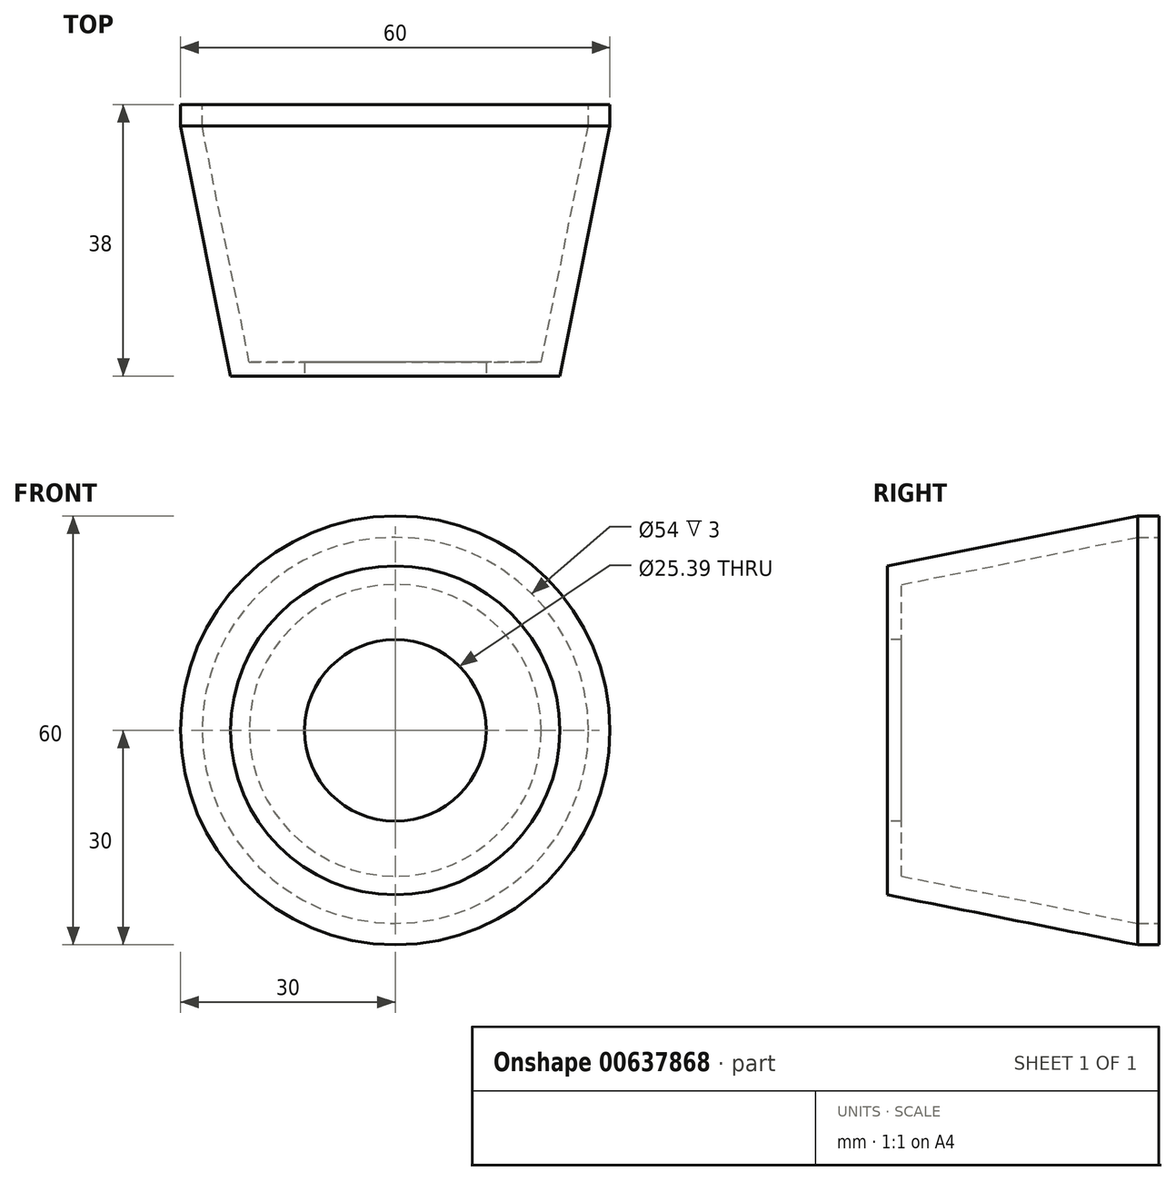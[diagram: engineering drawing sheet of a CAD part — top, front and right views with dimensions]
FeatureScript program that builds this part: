
annotation { "Feature Type Name" : "Feature", "Feature Type Description" : "" }
export const myFeature = defineFeature(function(context is Context, id is Id, definition is map)
    precondition{}
    {
        {
            var Q0;
            Q0=qCreatedBy(makeId("Front.planeOp"),FACE);
            var sketch = newSketch(context, id + "F0", { "sketchPlane" : qUnion([Q0])});
            skCircle(sketch, "E0", {"center": v(0, 0) * mm, "radius": 30 * mm});
            skCircle(sketch, "E1", {"center": v(0, 0) * mm, "radius": 27 * mm});
            skSolve(sketch);
        }
        {
            var Q0;
            Q0 = qSketchRegion(id + "F0", true);
            extrude(context, id + "F1", {"entities" : qUnion([Q0]), "depth" : 3 * mm, "offsetDistance" : 25 * mm});
        }
        {
            var Q0;
            Q0=qCreatedBy(makeId("Front.planeOp"),FACE);
            cPlane(context, id + "F2", {"entities" : qUnion([Q0]), "cplaneType" : CPlaneType.OFFSET, "offset" : 38 * mm, "width" : 150 * mm, "height" : 150 * mm});
        }
        {
            var Q0;
            Q0=qCreatedBy(id+"F2.planeOp",FACE);
            var sketch = newSketch(context, id + "F3", { "sketchPlane" : qUnion([Q0])});
            skCircle(sketch, "E2", {"center": v(0, 0) * mm, "radius": 23 * mm});
            skCircle(sketch, "E3", {"center": v(0, 0) * mm, "radius": 20 * mm, "construction": true});
            skSolve(sketch);
        }
        {
            var Q0;
            Q0=makeQuery(id+"F1.opExtrude","CAP_FACE",FACE,{"disambiguationData":[OSD([sQuery(id+"F0.wireOp",EDGE,"E0"),sQuery(id+"F0.wireOp",EDGE,"E1")])],"isStart":false});
            var sketch = newSketch(context, id + "F4", { "sketchPlane" : qUnion([Q0])});
            skCircle(sketch, "E4", {"center": v(0, 0) * mm, "radius": 30 * mm});
            skCircle(sketch, "E5", {"center": v(0, 0) * mm, "radius": 27 * mm, "construction": true});
            skSolve(sketch);
        }
        {
            var Q1;
            Q1 = qSketchRegion(id + "F4", true);
            var Q2;
            Q2 = qSketchRegion(id + "F3", true);
            loft(context, id + "F5", {"operationType" : NewBodyOperationType.ADD, "sheetProfilesArray" : [{ "sheetProfileEntities" : qUnion([Q1]) }, { "sheetProfileEntities" : qUnion([Q2]) }]});
        }
        {
            var Q0;
            Q0=makeQuery(id+"F5.opLoft","CAP_FACE",FACE,{"disambiguationData":[OSD([makeQuery(id+"F4.imprint","IMPRINT",FACE,{"disambiguationData":[TD([[makeQuery(id+"F4.imprint","IMPRINT",EDGE,{"derivedFrom":makeQuery(id+"F1.opExtrude","CAP_EDGE",EDGE,{"disambiguationData":[OSD([sQuery(id+"F0.wireOp",EDGE,"E1")])],"isStart":false})}),1.0]])]})])],"isStart":true});
            var sketch = newSketch(context, id + "F6", { "sketchPlane" : qUnion([Q0])});
            skCircle(sketch, "E6", {"center": v(0, 0) * mm, "radius": 27 * mm});
            skSolve(sketch);
        }
        {
            var Q0;
            Q0=makeQuery(id+"F5.opLoft","CAP_FACE",FACE,{"disambiguationData":[OSD([makeQuery(id+"F3.imprint","IMPRINT",FACE,{"disambiguationData":[TD([[makeQuery(id+"F3.imprint","IMPRINT",EDGE,{"derivedFrom":sQuery(id+"F3.wireOp",EDGE,"E2")}),1.0]])]})])],"isStart":true});
            var sketch = newSketch(context, id + "F7", { "sketchPlane" : qUnion([Q0])});
            skCircle(sketch, "E7", {"center": v(0, 0) * mm, "radius": 20 * mm});
            skSolve(sketch);
        }
        {
            var Q1;
            Q1 = qSketchRegion(id + "F7", true);
            var Q2;
            Q2 = qSketchRegion(id + "F6", true);
            loft(context, id + "F8", {"operationType" : NewBodyOperationType.REMOVE, "sheetProfilesArray" : [{ "sheetProfileEntities" : qUnion([Q1]) }, { "sheetProfileEntities" : qUnion([Q2]) }]});
        }
        {
            var Q0;
            Q0=makeQuery(id+"F5.opLoft","CAP_FACE",FACE,{"disambiguationData":[OSD([makeQuery(id+"F3.imprint","IMPRINT",FACE,{"disambiguationData":[TD([[makeQuery(id+"F3.imprint","IMPRINT",EDGE,{"derivedFrom":sQuery(id+"F3.wireOp",EDGE,"E2")}),1.0]])]})])],"isStart":true});
            var sketch = newSketch(context, id + "F9", { "sketchPlane" : qUnion([Q0])});
            skCircle(sketch, "E8", {"center": v(0, 0) * mm, "radius": 22.4 * mm});
            skCircle(sketch, "E9", {"center": v(0, 0) * mm, "radius": 12.7 * mm});
            skSolve(sketch);
        }
        {
            var Q0;
            Q0 = qSketchRegion(id + "F9", true);
            extrude(context, id + "F10", {"entities" : qUnion([Q0]), "operationType" : NewBodyOperationType.ADD, "oppositeDirection" : true, "depth" : 2 * mm, "offsetDistance" : 25 * mm});
        }
    });
